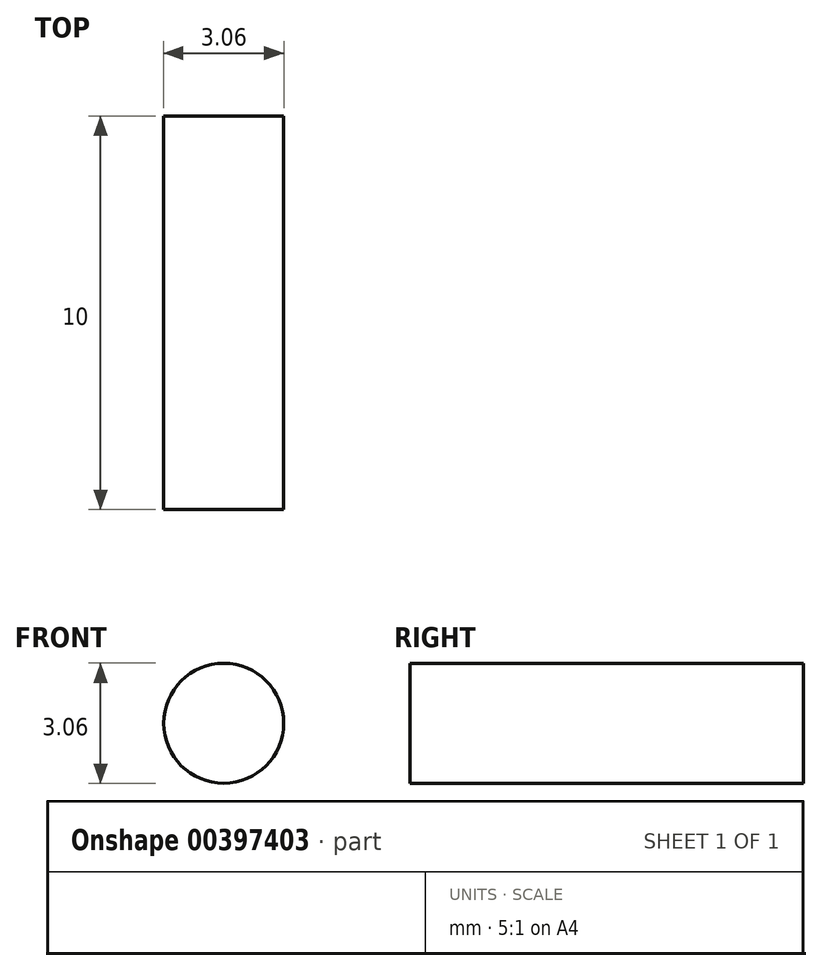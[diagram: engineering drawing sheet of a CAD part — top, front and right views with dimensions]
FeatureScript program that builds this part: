
annotation { "Feature Type Name" : "Feature", "Feature Type Description" : "" }
export const myFeature = defineFeature(function(context is Context, id is Id, definition is map)
    precondition{}
    {
        {
            var Q0;
            Q0=qCreatedBy(makeId("Front.planeOp"),FACE);
            var sketch = newSketch(context, id + "F0", { "sketchPlane" : qUnion([Q0])});
            skCircle(sketch, "E0", {"center": v(0, 0) * mm, "radius": 1.52 * mm});
            skSolve(sketch);
        }
        {
            var Q0;
            Q0 = qSketchRegion(id + "F0", true);
            extrude(context, id + "F1", {"entities" : qUnion([Q0]), "oppositeDirection" : true, "depth" : 10 * mm});
        }
    });
